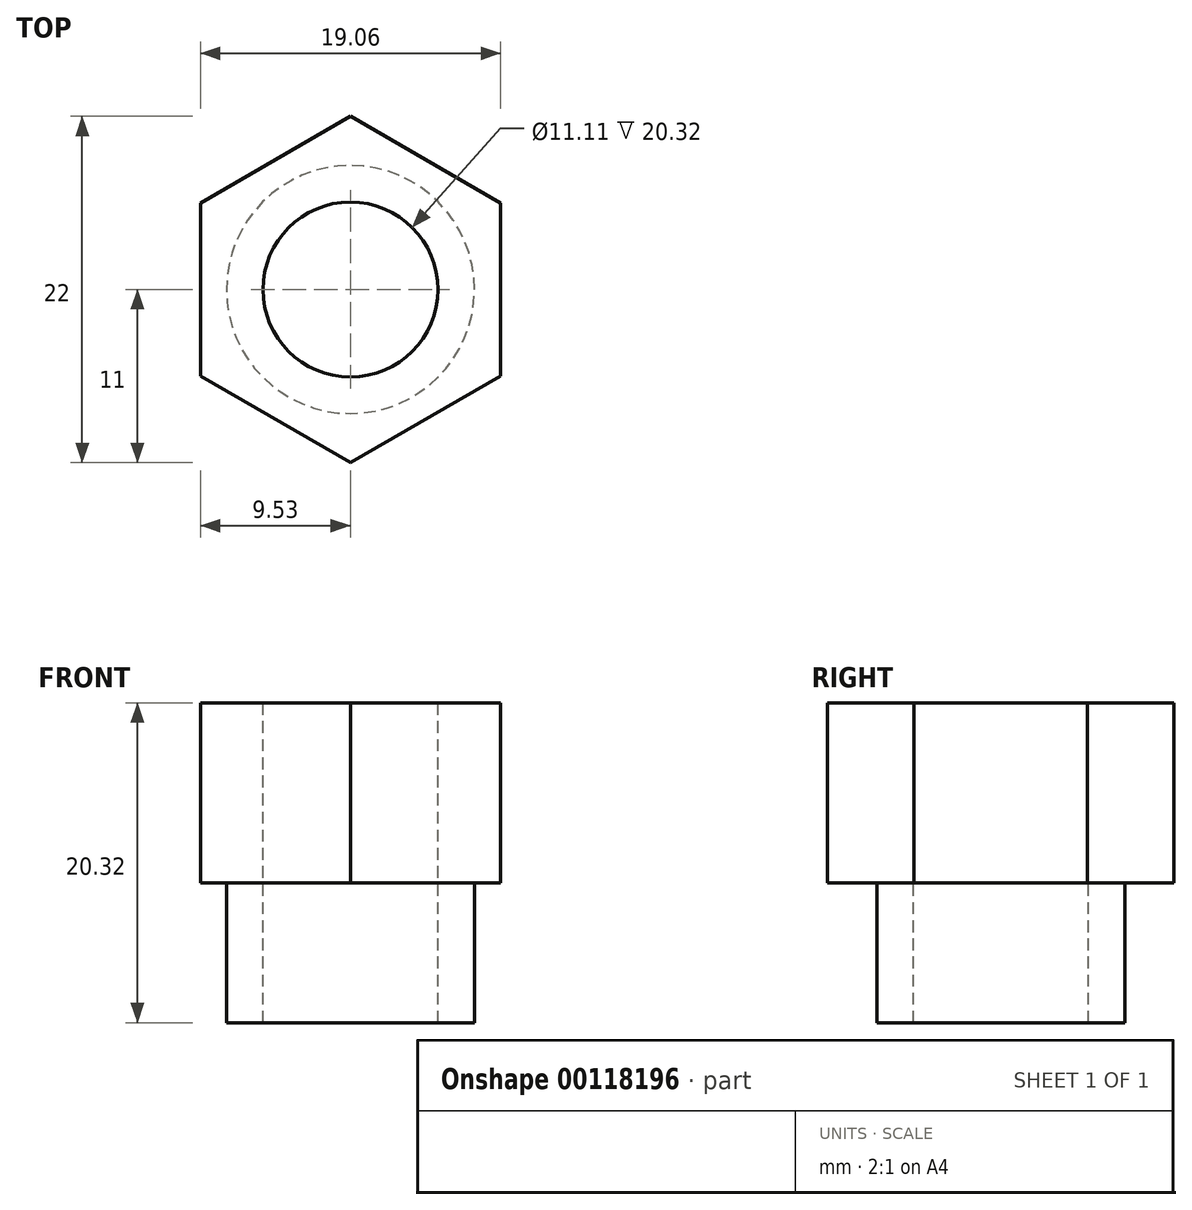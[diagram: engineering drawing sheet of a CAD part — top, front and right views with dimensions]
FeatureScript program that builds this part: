
annotation { "Feature Type Name" : "Feature", "Feature Type Description" : "" }
export const myFeature = defineFeature(function(context is Context, id is Id, definition is map)
    precondition{}
    {
        {
            var Q0;
            Q0=qCreatedBy(makeId("Top.planeOp"),FACE);
            var sketch = newSketch(context, id + "F0", { "sketchPlane" : qUnion([Q0])});
            skCircle(sketch, "E0.cCircle", {"center": v(0, 0) * mm, "radius": 9.52 * mm, "construction": true});
            skLineSegment(sketch, "E0.0", {"start": v(-9.53, -5.5) * mm, "end": v(-9.53, 5.5) * mm});
            skLineSegment(sketch, "E0.1", {"start": v(-9.52, 5.5) * mm, "end": v(0, 11) * mm});
            skLineSegment(sketch, "E0.2", {"start": v(0, 11) * mm, "end": v(9.52, 5.5) * mm});
            skLineSegment(sketch, "E0.3", {"start": v(9.52, 5.5) * mm, "end": v(9.53, -5.5) * mm});
            skLineSegment(sketch, "E0.4", {"start": v(9.53, -5.5) * mm, "end": v(0, -11) * mm});
            skLineSegment(sketch, "E0.5", {"start": v(0, -11) * mm, "end": v(-9.52, -5.5) * mm});
            skPoint(sketch, "E0.0.midPoint", {"position": v(-9.52, 0) * mm});
            skSolve(sketch);
        }
        {
            var Q0;
            Q0 = qSketchRegion(id + "F0", true);
            extrude(context, id + "F1", {"entities" : qUnion([Q0]), "oppositeDirection" : true, "depth" : 20.32 * mm});
        }
        {
            var Q0;
            Q0=qCreatedBy(makeId("Right.planeOp"),FACE);
            var sketch = newSketch(context, id + "F2", { "sketchPlane" : qUnion([Q0])});
            skLineSegment(sketch, "E1.bottom", {"start": v(-11, -20.32) * mm, "end": v(-7.87, -20.32) * mm});
            skLineSegment(sketch, "E1.top", {"start": v(-11, -11.43) * mm, "end": v(-7.87, -11.43) * mm});
            skLineSegment(sketch, "E1.left", {"start": v(-11, -20.32) * mm, "end": v(-11, -11.43) * mm});
            skLineSegment(sketch, "E1.right", {"start": v(-7.87, -20.32) * mm, "end": v(-7.87, -11.43) * mm});
            skSolve(sketch);
        }
        {
            var Q0;
            Q0=qCreatedBy(makeId("Right.planeOp"),FACE);
            var sketch = newSketch(context, id + "F3", { "sketchPlane" : qUnion([Q0])});
            skLineSegment(sketch, "E2", {"start": v(0, 14.55) * mm, "end": v(0, -30.75) * mm});
            skSolve(sketch);
        }
        {
            var Q0;
            Q0 = qSketchRegion(id + "F2", true);
            var Q1;
            Q1=sQuery(id+"F3.wireOp",EDGE,"E2");
            revolve(context, id + "F4", {"operationType" : NewBodyOperationType.REMOVE, "entities" : qUnion([Q0]), "axis" : qUnion([Q1]), "revolveType" : RevolveType.FULL, "oppositeDirection" : true});
        }
        {
            var Q0;
            Q0=makeQuery(id+"F1.opExtrude","CAP_FACE",FACE,{"disambiguationData":[OSD([sQuery(id+"F0.wireOp",EDGE,"E0.0"),sQuery(id+"F0.wireOp",EDGE,"E0.1"),sQuery(id+"F0.wireOp",EDGE,"E0.2"),sQuery(id+"F0.wireOp",EDGE,"E0.3"),sQuery(id+"F0.wireOp",EDGE,"E0.4"),sQuery(id+"F0.wireOp",EDGE,"E0.5")])],"isStart":true});
            var sketch = newSketch(context, id + "F5", { "sketchPlane" : qUnion([Q0])});
            skPoint(sketch, "E3", {"position": v(0, 0) * mm});
            skSolve(sketch);
        }
        {
            var Q0;
            Q0=sQuery(id+"F5.wireOp",VERTEX,"E3");
            var Q1;
            Q1=makeQuery(id+"F1.opExtrude","SWEPT_BODY",BODY,{"disambiguationData":[OSD([sQuery(id+"F0.wireOp",EDGE,"E0.0"),sQuery(id+"F0.wireOp",EDGE,"E0.1"),sQuery(id+"F0.wireOp",EDGE,"E0.2"),sQuery(id+"F0.wireOp",EDGE,"E0.3"),sQuery(id+"F0.wireOp",EDGE,"E0.4"),sQuery(id+"F0.wireOp",EDGE,"E0.5")])]});
            hole(context, id + "F6", {"style" : HoleStyle.SIMPLE, "endStyle" : HoleEndStyle.THROUGH, "holeDiameter" : 11.1 * mm, "locations" : qUnion([Q0]), "scope" : qUnion([Q1]), "isTappedThrough" : true});
        }
    });
